# Revit family: QF_ELECTROLUXPROFESSIONAL_1LSN95_WH6-20_E
name_source: partatom
category: Attrezzature speciali
units: mm (PartAtom-declared; Revit-internal decimal feet)

## family parameters
Basato su piano di lavoro = No
Condiviso = No
Punto di calcolo locali = No
Quota connettore circolare = Usa diametro
Sempre verticale = Sì
Taglio con vuoti quando caricato = No
Tipo di parte = Normale

## types (46) — shared parameters
Depth Actual = 947 mm  [stored 3.10696 ft]
Height Actual = 1412 mm  [stored 4.63255 ft]
Latent Heat Output = 0.0
Length Actual = 970 mm  [stored 3.18241 ft]
Modello = WH6-20
Produttore = Electrolux Professional
Sensible Heat Output = 0.0
URL = www.electroluxprofessional.com
Weight = 354
zero-valued in all types: Gas KW, Prospetto di default, Steam Pounds per Hour

## per-type parameters (varying)
| type | Cycle | Descrizione | Item Number | Phase | Volts | Watts |
| 9867930131 | 50 Hz | WASHER WH6-20 20KG EL 18KW 380-415/220-240/50/3N/3 COMPASS PRO 6H12 ML 2xWATER POWDER+5xLIQ. VALV.OPEN SILVER 2.I/O QC D | 1L0GBS | 3 | 415 V | 18500 W |
| 9867930161 | 60 Hz | WASHER WH6-20 20KG NO HEAT 220-240/60/1N COMPASS PRO 6L01 ML 2xWATER POWDER+5xLIQ. VALV.OPEN SST/SILVER EXT.PM. 2.I/O DI | 1L0GEC | 1 | 240 V | 2500 W |
| 9867930139 | 50 Hz | WASHER WH6-20 20KG EL 18KW 380-415/50/3N COMPASS PRO 6A01 SE 2xWATER POWDER+5xLIQ. VALV.OPEN SILVER 2.I/O DISCON. | 1LA1A0 | 3 | 415 V | 18500 W |
| 9867930129 | 50 Hz | WASHER WH6-20 20KG MOP 18KW 380-415/220-240/50/3N/3 COMPASS PRO 6M14 ML 2xWATER POWDER+5xLIQ. EL.VALV.OPEN SILVER 2.I/O | 1L0GA3 | 3 | 415 V | 18500 W |
| 9867930221 | 50 Hz | WASHER WH6-20 20KG EL 18KW 220-240/50/3 COMPASS PRO 6B01 ML 2xWATER POWDER+5xLIQ. VALV.OPEN SILVER 2.I/O DISCON. STOP | 1L0GZS | 3 | 240 V | 18500 W |
| 9867930136 | 50 Hz | WASHER WH6-20 20KG EL 18KW 380-415/50/3N COMPASS PRO 6G01 ML 2xWATER POWDER+5xLIQ. VALV.OPEN SST 2.I/O DISCON. STOP | 1L0GD3 | 3 | 415 V | 18500 W |
| 9867930119 | 50 Hz | WASHER WH6-20 20KG NO HEAT 220-240/50/1N COMPASS PRO 6L01 ML 2xWATER POWDER+5xLIQ. VALV.OPEN SILVER EXT.PM. 2.I/O DISCON | 1L8222 | 1 | 240 V | 2500 W |
| 9867930234 | 50 Hz | WASHER WH6-20 20KG EL 18KW 380-415/50/3N COMPASS PRO 6L01 ML 2xWATER POWDER+5xLIQ. VALV.OPEN SILVER EXT.PM. 2.I/O DISCON | 1LA25M | 3 | 415 V | 18500 W |
| 9867930279 | 50 Hz | WASHER WH6-20 20KG EL 18KW 380-415/50/3N COMPASS PRO 6G01 ML 2xWATER POWDER VALV.OPEN SST/SILVER DISCON. STOP | 1L0HJ9 | 3 | 415 V | 18500 W |
| 9867930067 | 50 Hz | WASHER WH6-20 20KG EL 18KW 380-415/220-240/50/3N/3 COMPASS PRO 6H01 ML 2xWATER POWDER+5xLIQ. EL.VALV.OPEN SILVER 2.I/O D | 1L824Z | 3 | 415 V | 18500 W |
| 9867930057 | 50 Hz | WASHER WH6-20 20KG EL 18KW 380-415/220-240/50/3N/3 COMPASS PRO 6H01 ML 2xWATER POWDER+5xLIQ. EL.VALV.OPEN SST/SILVER 2.I | 1L0H5C | 3 | 415 V | 18500 W |
| 9867930068 | 50 Hz | WASHER WH6-20 20KG MOP 18KW 380-415/50/3N COMPASS PRO 6M14 ML 2xWATER POWDER+5xLIQ. EL.VALV.OPEN SILVER 2.I/O DISCON. ST | 1L8250 | 3 | 415 V | 18500 W |
| 9867930058 | 50 Hz | WASHER WH6-20 20KG MOP 18KW 380-415/50/3N COMPASS PRO 6M14 ML 2xWATER POWDER+5xLIQ. EL.VALV.OPEN SST/SILVER 2.I/O DISCON | 1LSPKE | 3 | 415 V | 18500 W |
| 9867930123 | 50 Hz | WASHER WH6-20 20KG NO HEAT 200/50/60/3 COMPASS PRO 6H42 JP,EN 2xWATER POWDER+5xLIQ. VALV.OPEN SILVER 2.I/O DISCON. | 1L8226 | 3 | 200 V | 2500 W |
| 9867930097 | 50 Hz | WASHER WH6-20 20KG NO HEAT 200/50/60/3 COMPASS PRO 6H42 JP,EN 2xWATER POWDER+5xLIQ. VALV.OPEN SST/SILVER 2.I/O DISCON. | 1LA1BN | 3 | 200 V | 2500 W |
| 9867930237 | 50 Hz | WASHER WH6-20 20KG NO HEAT 220-240/50/1N COMPASS PRO 6L01 ML 2xWATER 5xLIQ. VALV.OPEN SILVER 2.I/O DISCON. | 1LSPRB | 1 | 240 V | 2500 W |
| 9867930217 | 50 Hz | WASHER WH6-20 20KG NO HEAT 220-240/50/1N COMPASS PRO 6L01 ML 2xWATER 5xLIQ. VALV.OPEN SILVER EXT.PM. 2.I/O DISCON. | 1LSPLY | 1 | 240 V | 2500 W |
| 9867930002 | 50 Hz | WH6-20 SG/SG/BL 18KW EX 8G01 | 1L0EYB | 3 | 415 V | 18500 W |
| 9867930247 | 50 Hz | WASHER WH6-20 20KG NO HEAT 220-240/50/1N COMPASS PRO 6L01 ML 2xWATER 5xLIQ. VALV.OPEN SILVER EXT.PM. 2.I/O DISCON. | 1L0H7V | 1 | 240 V | 2500 W |
| 9867930052 | 50 Hz | WASHER WH6-20 20KG EL 18KW 380-415/220-240/50/3N/3 COMPASS PRO 6G01 ML 2xWATER POWDER+5xLIQ. VALV.OPEN SST/SILVER 2.I/O | 1L0GEN | 3 | 415 V | 18500 W |
| 9867930092 | 50 Hz | WASHER WH6-20 20KG MOP 18KW 380-415/50/3N COMPASS PRO 6M16 ML 2xWATER POWDER+5xLIQ. EL.VALV.CLOSED SST/SILVER 2.I/O DISC | 1L0HG2 | 3 | 415 V | 18500 W |
| 9867930120 | 50 Hz | WASHER WH6-20 20KG MOP 18KW 380-415/50/3N COMPASS PRO 6M16 ML 2xWATER POWDER+5xLIQ. EL.VALV.CLOSED SILVER 2.I/O DISCON. | 1L8223 | 3 | 415 V | 18500 W |
| 9867930190 | 60 Hz | WASHER WH6-20 20KG NO HEAT 208-240/60/1 COMPASS PRO 6L01 ML 2xWATER POWDER+5xLIQ. VALV.OPEN SILVER ELS-NETW. 2.I/O | 1L0GP2 | 1 | 240 V | 2500 W |
| 9867930115 | 60 Hz | WASHER WH6-20 20KG EL 18KW 440/60/3 COMPASS PRO 6G01 ML 2xWATER POWDER+5xLIQ. VALV.OPEN SST/SILVER 2.I/O TRAFO DISCON. S | 1L8252 | 3 | 440 V | 18500 W |
| 9867930001 | 50 Hz | WH6-20 SG/SG/BL 18KW EX 8G01 | 1L0EYA | 3 | 415 V | 18500 W |
| 9867930138 | 50 Hz | WASHER WH6-20 20KG EL 18KW 380-400/220-230/50/3N/3 COMPASS PRO 6H12 SE 2xWATER POWDER+5xLIQ. VALV.OPEN SILVER 2.I/O QC D | 1LA19Z | 3 | 415 V | 18500 W |
| 9867930168 | 50 Hz | WASHER WH6-20 20KG EL 18KW 380-415/50/3N COMPASS PRO 6G01 CH-EN 2xWATER POWDER VALV.OPEN SILVER DISCON. STOP | 1L0GH6 | 3 | 415 V | 18500 W |
| 9867930155 | 50 Hz | WASHER WH6-20 20KG EL 18KW 380-415/50/3 COMPASS PRO 6G01 ML 2xWATER POWDER+5xLIQ. VALV.OPEN SILVER 2.I/O TRAFO DISCON. S | 1LSPBJ | 3 | 415 V | 18500 W |
| 9867930091 | 50 Hz | WASHER WH6-20 20KG NO HEAT 220-240/50/1N COMPASS PRO 6L01 ML 2xWATER POWDER+5xLIQ. VALV.OPEN SST/SILVER EXT.PM. 2.I/O DI | 1LA1B7 | 1 | 240 V | 2500 W |
| 9867930185 | 60 Hz | WASHER WH6-20 20KG EL 18KW 380-415/60/3 COMPASS PRO 6G07 ML 2xWATER POWDER+5xLIQ. VALV.OPEN SILVER 2.I/O TRAFO DISCON. S | 1LSPE8 | 3 | 415 V | 18500 W |
| 9867930004 | 50 Hz | WH6-20 SG/SG/BL 18KW EX 8G01 | 1L0EYD | 3 | 415 V | 18500 W |
| 9867930162 | 60 Hz | WASHER WH6-20 20KG EL 18KW 208-240/60/3 COMPASS PRO 6G01 ML 2xWATER POWDER+5xLIQ. VALV.CLOSED SST/SILVER 2.I/O DISCON. S | 1L0GES | 3 | 240 V | 18500 W |
| 9867930137 | 50 Hz | WASHER WH6-20 20KG EL 18KW 380-400/220-230/50/3N/3 COMPASS PRO 6H12 ML 2xWATER POWDER+5xLIQ. VALV.OPEN SST/SILVER 2.I/O | 1L0GD4 | 3 | 415 V | 18500 W |
| 9867930127 | 50 Hz | WASHER WH6-20 20KG MOP 18KW 380-415/50/3N COMPASS PRO 6M17 ML 2xWATER POWDER+5xLIQ. EL.VALV.CLOSED SILVER 2.I/O DISCON. | 1L0GAG | 3 | 415 V | 18500 W |
| 9867930003 | 50 Hz | WH6-20 SG/SG/BL 18KW EX 8G01 | 1L0EYC | 3 | 415 V | 18500 W |
| 9867930250 | 60 Hz | WASHER WH6-20 20KG NO HEAT 220/60/3 COMPASS PRO 6G01 ML 2xWATER POWDER+5xLIQ. VALV.CLOSED SILVER 2.I/O DISCON. STOP | 1L0HAM | 3 | 220 V | 2500 W |
| 9867930053 | 50 Hz | WASHER WH6-20 20KG EL 18KW 380-415/50/3N COMPASS PRO 6G01 ML 2xWATER POWDER+5xLIQ. VALV.OPEN SST/SILVER 2.I/O DISCON. ST | 1L0GDV | 3 | 415 V | 18500 W |
| 9867930147 | 50 Hz | WASHER WH6-20 20KG EL 18KW 220-230/50/3 COMPASS PRO 6G01 ML 2xWATER POWDER+5xLIQ. VALV.OPEN SILVER 2.I/O DISCON. STOP | 1LSP9M | 3 | 230 V | 18500 W |
| 9867930238 | 50 Hz | WASHER WH6-20 20KG NO HEAT 220-240/50/1N COMPASS PRO 6L07 ML 2xWATER 5xLIQ. VALV.OPEN SILVER 2.I/O DISCON. | 1LSPRK | 1 | 240 V | 2500 W |
| 9867930280 | 50 Hz | WASHER WH6-20 20KG NO HEAT 220-240/50/1N COMPASS PRO 6G01 CH-EN 2xWATER POWDER VALV.OPEN SILVER DISCON. STOP | 1L0HJA | 1 | 240 V | 2500 W |
| 9867930066 | 50 Hz | WASHER WH6-20 20KG EL 18KW 380-415/50/3N COMPASS PRO 6G01 ML 2xWATER POWDER+5xLIQ. VALV.OPEN SILVER 2.I/O DISCON. STOP | 1L824Y | 3 | 415 V | 18500 W |
| 9867930124 | 60 Hz | WASHER WH6-20 20KG EL 18KW 440/60/3 COMPASS PRO 6G01 ML 2xWATER POWDER+5xLIQ. VALV.OPEN SILVER 2.I/O TRAFO DISCON. STOP | 1L8227 | 3 | 440 V | 18500 W |
| 9867930154 | 60 Hz | WASHER WH6-20 20KG EL 18KW 480/60/3 COMPASS PRO 6G01 ML 2xWATER POWDER+5xLIQ. EL.VALV.OPEN SILVER 2.I/O TRAFO DISCON. ST | 1LSPBH | 3 | 480 V | 18500 W |
| 9867930144 | 50 Hz | WASHER WH6-20 20KG MOP 18KW 220-230/50/3 COMPASS PRO 6M14 ML 2xWATER POWDER+5xLIQ. EL.VALV.OPEN SILVER 2.I/O DISCON. STO | 1LA1B2 | 3 | 240 V | 18500 W |
| 9867930005 | 60 Hz | WH6-20 SG/SG HW EXUS 8Lxx | 1L0EYE | 1 | 240 V | 2500 W |
| 9867930065 | 50 Hz | WASHER WH6-20 20KG EL 18KW 380-415/220-240/50/3N/3 COMPASS PRO 6G01 ML 2xWATER POWDER+5xLIQ. VALV.OPEN SILVER 2.I/O DISC | 1L824K | 3 | 415 V | 18500 W |

note: [stored X ft] marks values corroborated as IEEE doubles in the binary element streams (Revit-internal decimal feet)

## geometry (parser evidence)
native form markers: Blend x4
no freeform markers — native parametric forms only
